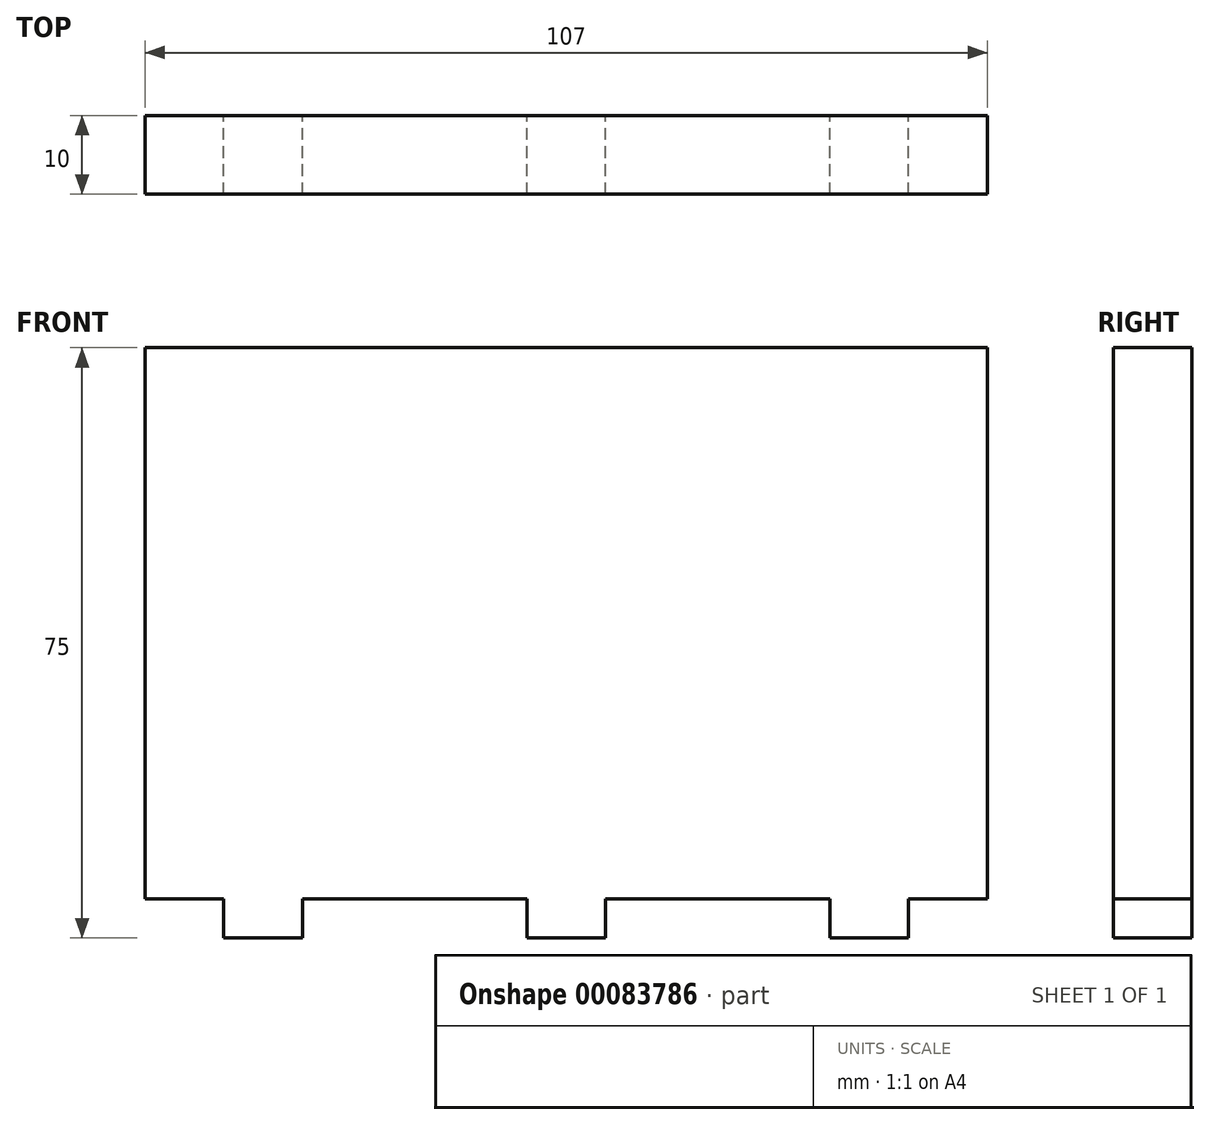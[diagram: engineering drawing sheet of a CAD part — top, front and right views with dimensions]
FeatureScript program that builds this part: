
annotation { "Feature Type Name" : "Feature", "Feature Type Description" : "" }
export const myFeature = defineFeature(function(context is Context, id is Id, definition is map)
    precondition{}
    {
        {
            var Q0;
            Q0=qCreatedBy(makeId("Front.planeOp"),FACE);
            var sketch = newSketch(context, id + "F0", { "sketchPlane" : qUnion([Q0])});
            skLineSegment(sketch, "E0.bottom", {"start": v(-53.5, 35) * mm, "end": v(53.5, 35) * mm});
            skLineSegment(sketch, "E0.left", {"start": v(-53.5, 35) * mm, "end": v(-53.5, -35) * mm});
            skLineSegment(sketch, "E0.right", {"start": v(53.5, 35) * mm, "end": v(53.5, -35) * mm});
            skPoint(sketch, "E0.middle", {"position": v(0, 0) * mm});
            skLineSegment(sketch, "E1.top", {"start": v(-43.5, -40) * mm, "end": v(-33.5, -40) * mm});
            skLineSegment(sketch, "E1.left", {"start": v(-43.5, -35) * mm, "end": v(-43.5, -40) * mm});
            skLineSegment(sketch, "E1.right", {"start": v(-33.5, -35) * mm, "end": v(-33.5, -40) * mm});
            skLineSegment(sketch, "E2.top", {"start": v(-5, -40) * mm, "end": v(5, -40) * mm});
            skLineSegment(sketch, "E2.left", {"start": v(-5, -35) * mm, "end": v(-5, -40) * mm});
            skLineSegment(sketch, "E2.right", {"start": v(5, -35) * mm, "end": v(5, -40) * mm});
            skLineSegment(sketch, "E3.MirrorCS", {"start": v(43.5, -35) * mm, "end": v(43.5, -40) * mm});
            skLineSegment(sketch, "E4.MirrorCS", {"start": v(33.5, -35) * mm, "end": v(33.5, -40) * mm});
            skLineSegment(sketch, "E5.MirrorCS", {"start": v(43.5, -40) * mm, "end": v(33.5, -40) * mm});
            skLineSegment(sketch, "E6.trimOffspring", {"start": v(-33.5, -35) * mm, "end": v(-5, -35) * mm});
            skLineSegment(sketch, "E7.trimOffspring", {"start": v(43.5, -35) * mm, "end": v(53.5, -35) * mm});
            skLineSegment(sketch, "E8.trimOffspring", {"start": v(5, -35) * mm, "end": v(33.5, -35) * mm});
            skLineSegment(sketch, "E9", {"start": v(-43.5, -35) * mm, "end": v(-53.5, -35) * mm});
            skSolve(sketch);
        }
        {
            var Q0;
            Q0 = qSketchRegion(id + "F0", true);
            extrude(context, id + "F1", {"entities" : qUnion([Q0]), "depth" : 10 * mm});
        }
    });
